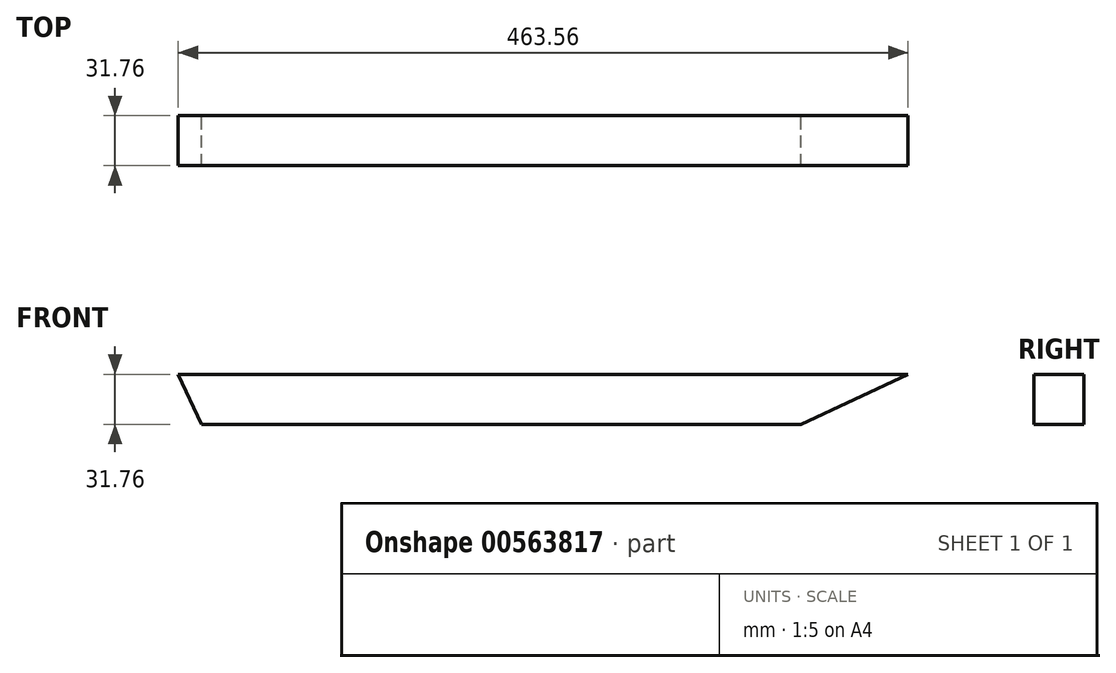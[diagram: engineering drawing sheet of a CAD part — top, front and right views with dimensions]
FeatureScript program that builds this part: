
annotation { "Feature Type Name" : "Feature", "Feature Type Description" : "" }
export const myFeature = defineFeature(function(context is Context, id is Id, definition is map)
    precondition{}
    {
        {
            var Q0;
            Q0=qCreatedBy(makeId("Front.planeOp"),FACE);
            var sketch = newSketch(context, id + "F0", { "sketchPlane" : qUnion([Q0])});
            skLineSegment(sketch, "E0.bottom", {"start": v(-231.78, 15.87) * mm, "end": v(231.78, 15.87) * mm});
            skLineSegment(sketch, "E0.top", {"start": v(-231.78, -15.88) * mm, "end": v(231.78, -15.88) * mm});
            skLineSegment(sketch, "E0.left", {"start": v(-231.78, 15.87) * mm, "end": v(-231.78, -15.88) * mm});
            skLineSegment(sketch, "E0.right", {"start": v(231.78, 15.87) * mm, "end": v(231.78, -15.88) * mm});
            skPoint(sketch, "E0.middle", {"position": v(0, 0) * mm});
            skLineSegment(sketch, "E1", {"start": v(-231.77, 15.88) * mm, "end": v(-216.97, -15.87) * mm});
            skLineSegment(sketch, "E2", {"start": v(231.78, 15.87) * mm, "end": v(163.69, -15.88) * mm});
            skSolve(sketch);
        }
        {
            var Q0;
            Q0=makeQuery(id+"F0.imprint","IMPRINT",FACE,{"disambiguationData":[TD([[makeQuery(id+"F0.imprint","IMPRINT",EDGE,{"derivedFrom":sQuery(id+"F0.wireOp",EDGE,"E0.bottom")}),-1.0]])]});
            extrude(context, id + "F1", {"entities" : qUnion([Q0]), "endBound" : BoundingType.SYMMETRIC, "depth" : 31.75 * mm, "offsetDistance" : 25.4 * mm});
        }
    });
